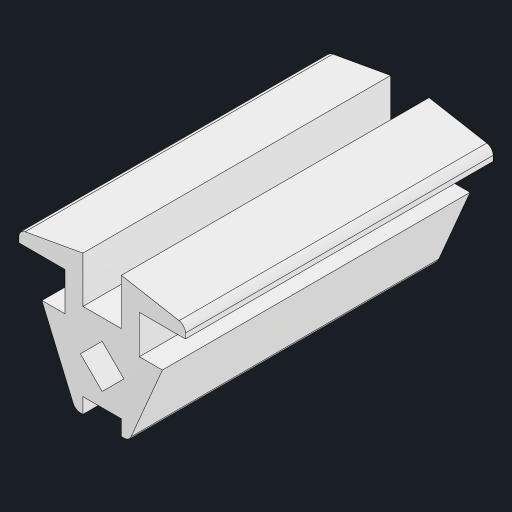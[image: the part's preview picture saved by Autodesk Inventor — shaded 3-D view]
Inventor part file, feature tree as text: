
AUTODESK INVENTOR PART (.ipt)
format: ipt  version: 2023 (Build 270158000, 158)  size: 165,888 bytes
history: native  units: mm
features: other x1, extrude x1, fillet x1, sketch x1
ambient origin geometry x8: Origin, YZ Plane, XZ Plane, XY Plane, X Axis, Y Axis, Z Axis, Center Point
bodies: Body1 (feature_tree)
feature tree (4):
  other  "ソリッド1"
  extrude  "押し出し1"  Depth=40.0mm TaperAngle=0.0deg
  fillet  "フィレット2"  Radius=2.0mm
  sketch  "スケッチ1"
